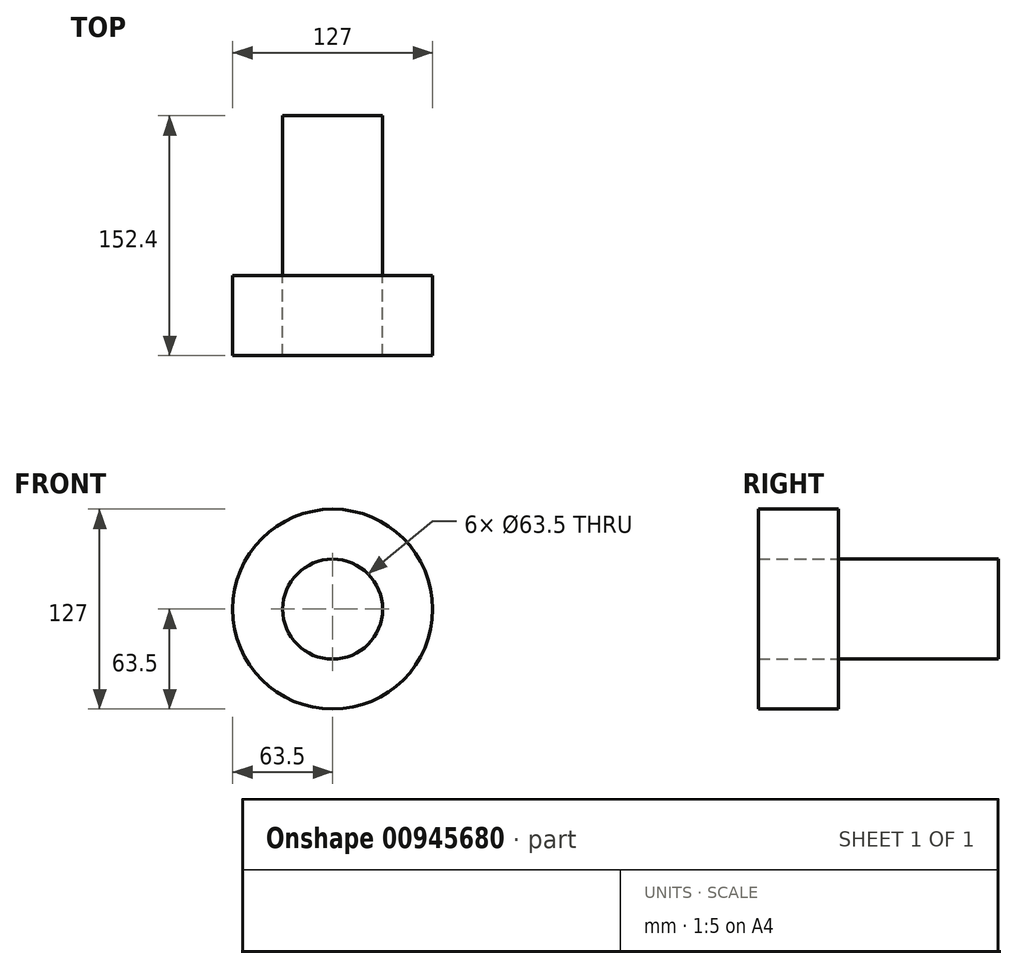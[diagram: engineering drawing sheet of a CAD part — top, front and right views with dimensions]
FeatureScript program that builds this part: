
annotation { "Feature Type Name" : "Feature", "Feature Type Description" : "" }
export const myFeature = defineFeature(function(context is Context, id is Id, definition is map)
    precondition{}
    {
        {
            var Q0;
            Q0=qCreatedBy(makeId("Front.planeOp"),FACE);
            var sketch = newSketch(context, id + "F0", { "sketchPlane" : qUnion([Q0])});
            skCircle(sketch, "E0", {"center": v(0, 0) * mm, "radius": 31.75 * mm});
            skSolve(sketch);
        }
        {
            var Q0;
            Q0=makeQuery(id+"F0.imprint","IMPRINT",FACE,{"disambiguationData":[TD([[makeQuery(id+"F0.imprint","IMPRINT",EDGE,{"derivedFrom":sQuery(id+"F0.wireOp",EDGE,"E0")}),1.0]])]});
            extrude(context, id + "F1", {"entities" : qUnion([Q0]), "depth" : 101.6 * mm, "offsetDistance" : 25.4 * mm});
        }
        {
            var Q0;
            Q0=makeQuery(id+"F1.opExtrude","CAP_FACE",FACE,{"disambiguationData":[OSD([sQuery(id+"F0.wireOp",EDGE,"E0")])],"isStart":false});
            var sketch = newSketch(context, id + "F2", { "sketchPlane" : qUnion([Q0])});
            skCircle(sketch, "E1", {"center": v(0, 0) * mm, "radius": 63.5 * mm});
            skSolve(sketch);
        }
        {
            var Q0;
            Q0=makeQuery(id+"F2.imprint","IMPRINT",FACE,{"disambiguationData":[TD([[makeQuery(id+"F2.imprint","IMPRINT",EDGE,{"derivedFrom":sQuery(id+"F2.wireOp",EDGE,"E1")}),1.0]])]});
            extrude(context, id + "F3", {"entities" : qUnion([Q0]), "depth" : 50.8 * mm, "offsetDistance" : 25.4 * mm});
        }
        {
            var Q0;
            Q0=makeQuery(id+"F1.opExtrude","CAP_FACE",FACE,{"disambiguationData":[OSD([sQuery(id+"F0.wireOp",EDGE,"E0")])],"isStart":false});
            extrude(context, id + "F4", {"entities" : qUnion([Q0]), "depth" : 50.8 * mm, "offsetDistance" : 25.4 * mm});
        }
    });
